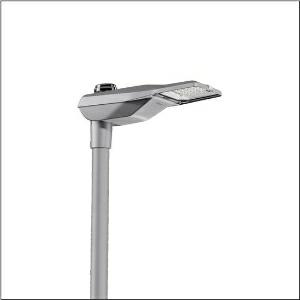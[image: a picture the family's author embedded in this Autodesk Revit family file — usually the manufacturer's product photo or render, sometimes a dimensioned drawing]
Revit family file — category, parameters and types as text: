
# Revit family: streetlight_sl_21_micro___st1_5a_5xe5p37n08db_dfc7
name_source: partatom
category: Lighting Fixtures
units: mm (PartAtom-declared; Revit-internal decimal feet)

## family parameters
Cut with Voids When Loaded = No
Host = Face
Light Source = No
Part Type = Normal
Room Calculation Point = No
Round Connector Dimension = Use Diameter
Shared = No

## types (1)
- --- (1 x LED, 5020 lm, 39.1 W, 3000K)
    Apparent Load = 39 VA
    CIE Flux Codes = 22 53 95 100 100
    Color Rendering = 70
    Color Temperature = 3000K
    Default Elevation = 1800 mm
    Description = Streetlight SL 21 micro, mast luminaire, primary light control with lens, of PMMA, primary optical cover: cover, of toughened safety glass, transparent, light distribution: ST1.5a, light emission: direct distribution, primary light characteristic: asymmetric, installation type: post-top, LED, 3G 1.5mm², High Power LED, rated luminous flux: 5.020lm, luminous efficacy: 128lm/W, light colour: 730, colour temperature: 3000K, control gear: NEMA (7pin), control: overheat protection, pre-setting: linear dimming characteristic, constant luminous flux control, time-dependent luminous flux control, flexible luminous flux parameterisation, mains connection: 230..240V, AC, 50/60Hz, connection cable pre-assembled, cable length: 6,5m, wiring characteristics: H07RN-F, start of lifetime: 39W, end of service life: 41W, reduction: 18W, luminaire housing, of diecast aluminium (EN AC-44300), powder-coated, SITECO metallic grey (DB 702S), corrosivity category C5 high according to DIN EN ISO 12944, multi-level sealing system, sealing non-destructively replaceable, inclination adjustable: 0°, 5°, 10°, 15°, length: 528mm, width: 235mm, height: 110mm, spigot size: 76/60mm (post-top), mounting height: 4..8m, protection rating (complete): IP66, insulation class (complete): insulation class I (protective earthing), certification: CE, ENEC, ENEC+, VDE, impact resistance: IK10, permissible operating ambient temperature for outdoor applications: -40..+50°C, standard-compliant lighting for roads and squares, packaging unit: 1 piece

Light Distribution: ST1.5a
    Height = 110 mm
    Lamp = 1 x LED
    Lamp Light Flux = 5020 lm
    Lamp Power = 39.1 W
    Lamp count = 1
    Length = 528 mm
    Luminous efficacy = 128 lm/W
    Manufacturer = Siteco
    ModVariant = No
    Model = 5XE5P37N08DB
    Number of Poles = 1
    OnlyDefault = Yes
    Power Factor = 1
    Product Name = Streetlight SL 21 micro | ST1.5a
    Product group = mast luminaire | pylon top
    ProductGroupID = 6100
    Protection Class = Protection class I
    Protection Degree = IP 66
    RLX_Detail_Level = 1
    RLX_Emergency_Light_Flux = 0 lm
    RLX_Emergency_Type = 0
    RLX_Emergency_Type_DB = No
    RlxData = <blob elided: 103589 chars, md5=cb30a8dd>
    Socket = socket
    Standby Power = 0 W
    System Light Flux = 5020 lm
    System Power = 39 W
    Type Comments = factory setting: luminous flux: 100 % | dim-lin: 254 | 765 mA
    Type Image = l_1294375.jpg
    URL = http://relux.com
    VarID = @adj_133261
    Voltage = 0 V
    Weight = 0.00 kg
    Width = 235 mm

## geometry (parser evidence)
native form markers: Blend x4, Sweep x11
no freeform markers — native parametric forms only
